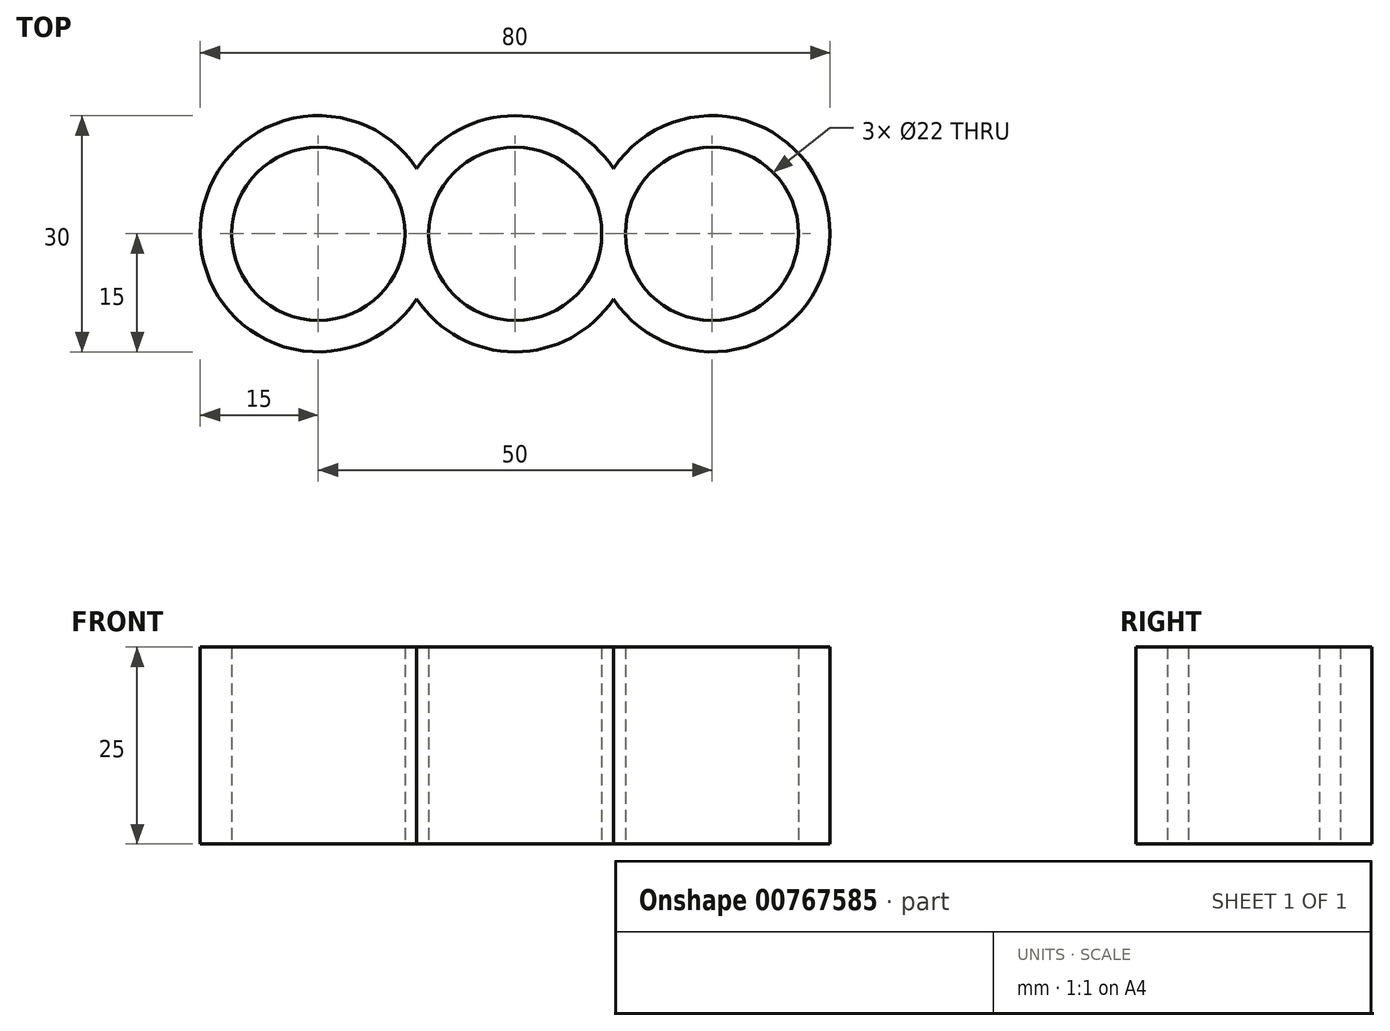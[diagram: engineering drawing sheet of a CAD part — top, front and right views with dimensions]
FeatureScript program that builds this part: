
annotation { "Feature Type Name" : "Feature", "Feature Type Description" : "" }
export const myFeature = defineFeature(function(context is Context, id is Id, definition is map)
    precondition{}
    {
        {
            var Q0;
            Q0=qCreatedBy(makeId("Top.planeOp"),FACE);
            var sketch = newSketch(context, id + "F0", { "sketchPlane" : qUnion([Q0])});
            skArc(sketch, "E0", {"start": v(0, 11) * mm, "mid": v(-11, 0) * mm, "end": v(0, -11) * mm});
            skArc(sketch, "E1", {"start": v(-12.5, -8.3) * mm, "mid": v(-7.1, -13.22) * mm, "end": v(0, -15) * mm});
            skArc(sketch, "E2", {"start": v(-14.58, 3.52) * mm, "mid": v(-36, 0) * mm, "end": v(-14.58, -3.52) * mm});
            skArc(sketch, "E3.trimOffspring", {"start": v(-12.5, 8.3) * mm, "mid": v(-40, 0) * mm, "end": v(-12.5, -8.3) * mm});
            skArc(sketch, "E4", {"start": v(-14.58, -3.52) * mm, "mid": v(-14, 0) * mm, "end": v(-14.58, 3.52) * mm});
            skLineSegment(sketch, "E5", {"start": v(0, -11) * mm, "end": v(0, -15) * mm});
            skArc(sketch, "E6.trimOffspring", {"start": v(0, 15) * mm, "mid": v(-7.1, 13.22) * mm, "end": v(-12.5, 8.3) * mm});
            skPoint(sketch, "E7.orphan", {"position": v(0, 21.55) * mm});
            skArc(sketch, "E8.MirrorCS", {"start": v(12.5, 8.3) * mm, "mid": v(40, 0) * mm, "end": v(12.5, -8.3) * mm});
            skArc(sketch, "E9.MirrorCS", {"start": v(14.58, 3.52) * mm, "mid": v(36, 0) * mm, "end": v(14.58, -3.52) * mm});
            skArc(sketch, "E10.MirrorCS", {"start": v(14.58, -3.52) * mm, "mid": v(14, 0) * mm, "end": v(14.58, 3.52) * mm});
            skArc(sketch, "E11.MirrorCS", {"start": v(0, 11) * mm, "mid": v(11, 0) * mm, "end": v(0, -11) * mm});
            skArc(sketch, "E12.MirrorCS", {"start": v(0, 15) * mm, "mid": v(7.1, 13.22) * mm, "end": v(12.5, 8.3) * mm});
            skArc(sketch, "E13.MirrorCS", {"start": v(12.5, -8.3) * mm, "mid": v(7.1, -13.22) * mm, "end": v(0, -15) * mm});
            skSolve(sketch);
        }
        {
            var Q0;
            Q0 = qSketchRegion(id + "F0", true);
            extrude(context, id + "F1", {"entities" : qUnion([Q0]), "depth" : 25 * mm, "offsetDistance" : 25 * mm});
        }
    });
